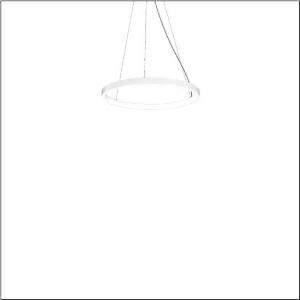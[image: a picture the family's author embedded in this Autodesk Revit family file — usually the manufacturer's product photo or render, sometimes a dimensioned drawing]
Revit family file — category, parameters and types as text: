
# Revit family: silica_r__21_ring-i_5pjbi1d1004a_4ad1
name_source: partatom
category: Lighting Fixtures
units: mm (PartAtom-declared; Revit-internal decimal feet)

## family parameters
Cut with Voids When Loaded = No
Host = Face
Light Source = No
Part Type = Normal
Room Calculation Point = No
Round Connector Dimension = Use Diameter
Shared = No

## types (1)
- Silica® 21 Ring-I (1 x LED, 3430 lm, 60 W, 3000K)
    Apparent Load = 60 VA
    CIE Flux Codes = 22 48 76 50 101
    Color Rendering = 80
    Color Temperature = 3000K
    Default Elevation = 1800 mm
    Description = Silica® 21 Ring-I, suspended luminaire, of PMMA, frosted, light emission: inner ring side luminous distribution, primary light characteristic: symmetric, installation type: suspended mounting, LED, rated luminous flux: 3.430lm, luminous efficacy: 57lm/W, light colour: 830, colour temperature: 3000K, control gear: DALI 2, with terminal, 5-pole, mains connection: 230V, AC/DC, 0/50..60Hz, rated input power: 60W, housing, of extruded aluminium section, traffic white (RAL 9016), diameter: 610mm, ceiling canopy, traffic white (RAL 9016), protection rating (lamp compartment): IP40, insulation class (complete): insulation class I (protective earthing), certification: CE, impact resistance: IK02, permissible operating ambient temperature: 0..+35°C, packaging unit: 1 piece
    Height = 48 mm  [stored 0.15748 ft]
    Lamp = 1 x LED
    Lamp Light Flux = 3430 lm
    Lamp Power = 60 W
    Lamp count = 1
    Length = 610 mm
    Luminous efficacy = 57 lm/W
    Manufacturer = Siteco
    ModVariant = No
    Model = 5PJBI1D1004A
    Mounting Place = Ceiling
    Mounting Type = Pendant
    Number of Poles = 1
    OnlyDefault = Yes
    Power Factor = 1
    Product Name = Silica® 21 Ring-I
    Product group = suspended luminaire
    ProductGroupID = 905
    Protection Class = Protection class I
    Protection Degree = IP 40
    RLX_Detail_Level = 1
    RLX_Emergency_Light_Flux = 0 lm
    RLX_Emergency_Type = 0
    RLX_Emergency_Type_DB = No
    RlxData = <blob elided: 10497 chars, md5=8d5d9916>
    Socket = socket
    Standby Power = 0 W
    System Light Flux = 3430 lm
    System Power = 60 W
    Type Comments = Product without accessories
    Type Image = l_1258363.jpg
    URL = http://relux.com
    VarID = ---
    Voltage = 0 V
    Weight = 0.00 kg
    Width = 0 mm  [stored 0 ft]

note: [stored X ft] marks values corroborated as IEEE doubles in the binary element streams (Revit-internal decimal feet)

## geometry (parser evidence)
native form markers: Sweep x11
no freeform markers — native parametric forms only
